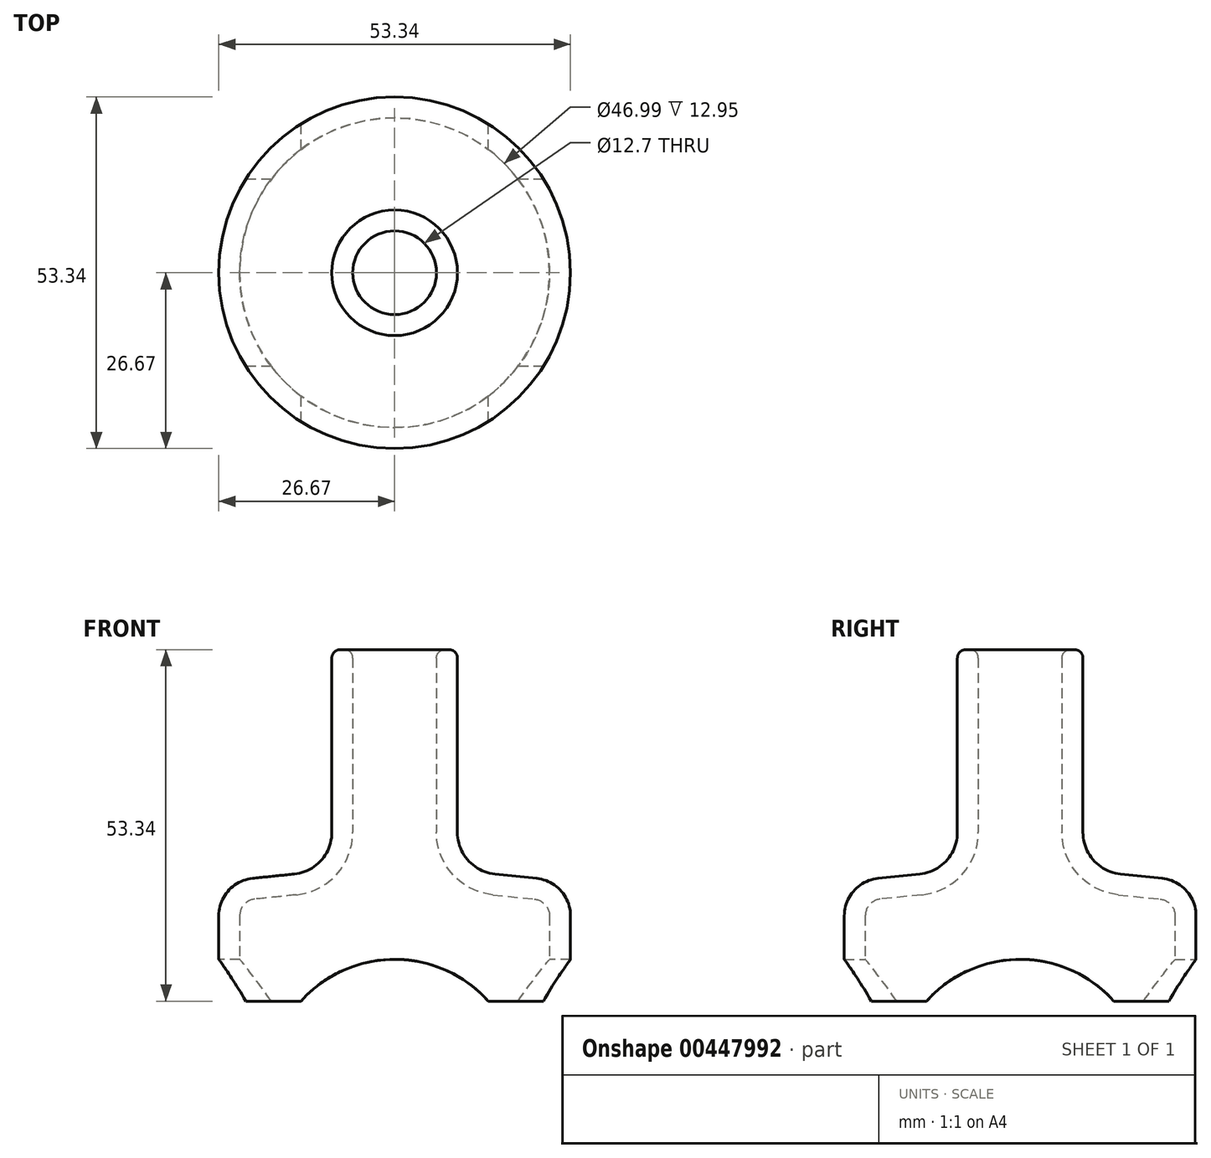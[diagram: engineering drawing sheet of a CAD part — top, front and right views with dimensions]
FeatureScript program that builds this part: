
annotation { "Feature Type Name" : "Feature", "Feature Type Description" : "" }
export const myFeature = defineFeature(function(context is Context, id is Id, definition is map)
    precondition{}
    {
        {
            var Q0;
            Q0=qCreatedBy(makeId("Front.planeOp"),FACE);
            var sketch = newSketch(context, id + "F0", { "sketchPlane" : qUnion([Q0])});
            skLineSegment(sketch, "E0", {"start": v(0, 0) * mm, "end": v(0, 53.34) * mm, "construction": true});
            skLineSegment(sketch, "E1", {"start": v(0, 53.34) * mm, "end": v(6.35, 53.34) * mm, "construction": true});
            skLineSegment(sketch, "E2", {"start": v(6.35, 52.07) * mm, "end": v(6.35, 25.6) * mm});
            skLineSegment(sketch, "E3", {"start": v(14.9, 16.13) * mm, "end": v(21.22, 15.48) * mm});
            skLineSegment(sketch, "E4", {"start": v(23.5, 12.95) * mm, "end": v(23.5, 0) * mm});
            skLineSegment(sketch, "E5.0", {"start": v(26.67, 12.95) * mm, "end": v(26.67, 0) * mm});
            skLineSegment(sketch, "E5.1", {"start": v(15.22, 19.29) * mm, "end": v(21.54, 18.63) * mm});
            skLineSegment(sketch, "E5.2", {"start": v(9.52, 52.07) * mm, "end": v(9.52, 25.6) * mm});
            skLineSegment(sketch, "E6", {"start": v(7.62, 53.34) * mm, "end": v(8.25, 53.34) * mm});
            skLineSegment(sketch, "E7", {"start": v(23.5, 0) * mm, "end": v(26.67, 0) * mm});
            skPoint(sketch, "E8.visualSharp", {"position": v(9.52, 19.88) * mm});
            skArc(sketch, "E8.filletArc", {"start": v(9.53, 25.6) * mm, "mid": v(11.16, 21.35) * mm, "end": v(15.22, 19.29) * mm});
            skPoint(sketch, "E9.visualSharp", {"position": v(6.35, 17.02) * mm});
            skArc(sketch, "E9.filletArc", {"start": v(6.35, 25.6) * mm, "mid": v(8.8, 19.23) * mm, "end": v(14.9, 16.13) * mm});
            skPoint(sketch, "E10.visualSharp", {"position": v(23.5, 15.24) * mm});
            skArc(sketch, "E10.filletArc", {"start": v(23.5, 12.95) * mm, "mid": v(22.84, 14.65) * mm, "end": v(21.22, 15.48) * mm});
            skPoint(sketch, "E11.visualSharp", {"position": v(26.67, 18.1) * mm});
            skArc(sketch, "E11.filletArc", {"start": v(26.67, 12.95) * mm, "mid": v(25.2, 16.78) * mm, "end": v(21.54, 18.63) * mm});
            skPoint(sketch, "E12.visualSharp", {"position": v(6.35, 53.34) * mm});
            skArc(sketch, "E12.filletArc", {"start": v(7.62, 53.34) * mm, "mid": v(6.72, 52.97) * mm, "end": v(6.35, 52.07) * mm});
            skPoint(sketch, "E13.visualSharp", {"position": v(9.52, 53.34) * mm});
            skArc(sketch, "E13.filletArc", {"start": v(9.52, 52.07) * mm, "mid": v(9.15, 52.97) * mm, "end": v(8.25, 53.34) * mm});
            skSolve(sketch);
        }
        {
            var Q0;
            Q0 = qSketchRegion(id + "F0", true);
            var Q1;
            Q1=sQuery(id+"F0.wireOp",EDGE,"E0");
            revolve(context, id + "F1", {"entities" : qUnion([Q0]), "axis" : qUnion([Q1]), "revolveType" : RevolveType.FULL});
        }
        {
            var Q0;
            Q0=qCreatedBy(makeId("Front.planeOp"),FACE);
            var sketch = newSketch(context, id + "F2", { "sketchPlane" : qUnion([Q0])});
            skCircle(sketch, "E14", {"center": v(0, -12.7) * mm, "radius": 19.05 * mm});
            skSolve(sketch);
        }
        {
            var Q0;
            Q0=makeQuery(id+"F2.imprint","IMPRINT",FACE,{"disambiguationData":[TD([[makeQuery(id+"F2.imprint","IMPRINT",EDGE,{"derivedFrom":sQuery(id+"F2.wireOp",EDGE,"E14")}),1.0]])]});
            extrude(context, id + "F3", {"entities" : qUnion([Q0]), "operationType" : NewBodyOperationType.REMOVE, "endBound" : BoundingType.SYMMETRIC, "depth" : 76.2 * mm});
        }
        {
            var Q0;
            Q0=qCreatedBy(makeId("Right.planeOp"),FACE);
            var sketch = newSketch(context, id + "F4", { "sketchPlane" : qUnion([Q0])});
            skCircle(sketch, "E15", {"center": v(0, -12.7) * mm, "radius": 19.05 * mm});
            skSolve(sketch);
        }
        {
            var Q0;
            Q0=makeQuery(id+"F4.imprint","IMPRINT",FACE,{"disambiguationData":[TD([[makeQuery(id+"F4.imprint","IMPRINT",EDGE,{"derivedFrom":sQuery(id+"F4.wireOp",EDGE,"E15")}),1.0]])]});
            extrude(context, id + "F5", {"entities" : qUnion([Q0]), "operationType" : NewBodyOperationType.REMOVE, "endBound" : BoundingType.SYMMETRIC, "depth" : 76.2 * mm});
        }
    });
